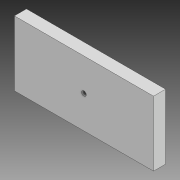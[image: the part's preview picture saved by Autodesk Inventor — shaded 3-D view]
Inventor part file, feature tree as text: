
AUTODESK INVENTOR PART (.ipt)
format: ipt  version: 2020 (Build 240168000, 168)  size: 113,152 bytes
history: native  units: mm
features: extrude x3, sketch x3, projected_geometry x1
ambient origin geometry x8: Origin, YZ Plane, XZ Plane, XY Plane, X Axis, Y Axis, Z Axis, Center Point
bodies: Solid1 (feature_tree)
feature tree (7):
  extrude  "Extrusion1"  Depth=70.0mm
  extrude  "Extrusion3"  Depth=10.0mm TaperAngle=0.0deg
  extrude  "Extrusion4"  Depth=3.0mm
  sketch  "Sketch1"  dims[d0=50.0mm d2=70.0mm]
  sketch  "Sketch3"  dims[d3=150.0mm d4=10.0mm d5=0.0mm]
  sketch  "Sketch4"  dims[d10=50.0mm d11=40.0mm d12=0.0mm d13=0.0mm d14=5.0mm d15=3.0mm d16=0.0mm]
  projected_geometry  "Projected Loop1"
